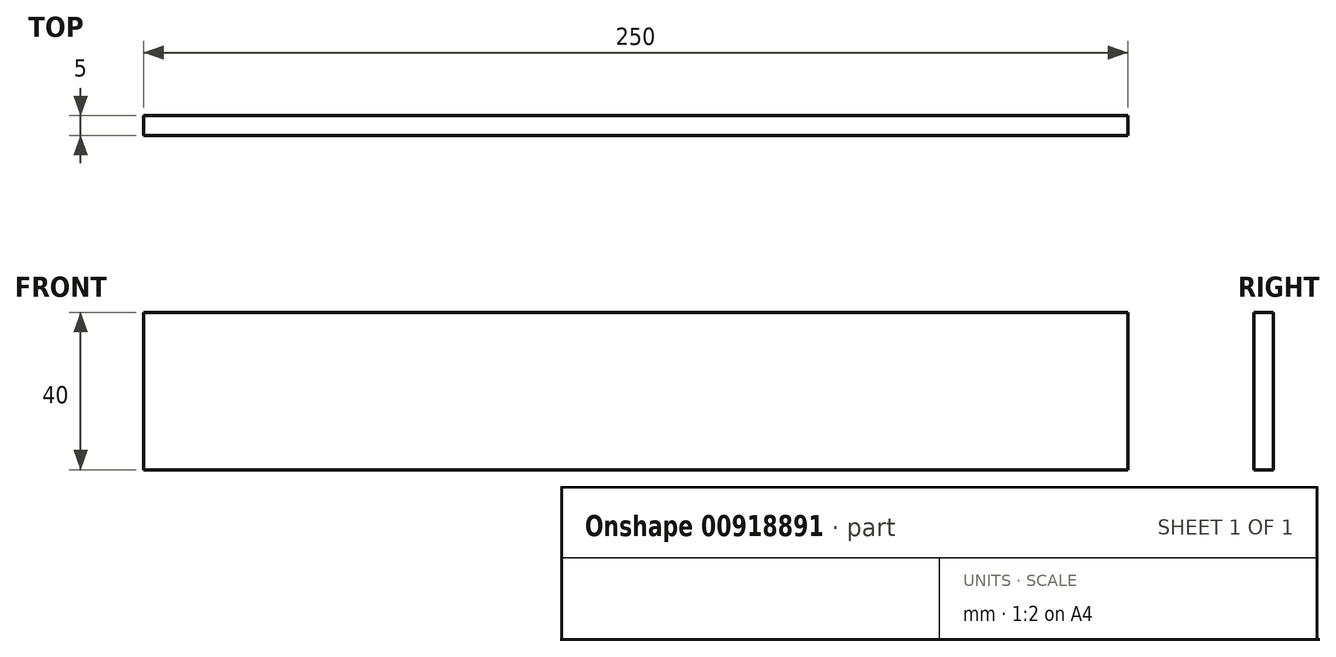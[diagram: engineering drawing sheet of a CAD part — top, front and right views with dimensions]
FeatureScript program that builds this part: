
annotation { "Feature Type Name" : "Feature", "Feature Type Description" : "" }
export const myFeature = defineFeature(function(context is Context, id is Id, definition is map)
    precondition{}
    {
        {
            var Q0;
            Q0=qCreatedBy(makeId("Front.planeOp"),FACE);
            var sketch = newSketch(context, id + "F0", { "sketchPlane" : qUnion([Q0])});
            skLineSegment(sketch, "E0.bottom", {"start": v(-129.94, -72.08) * mm, "end": v(120.06, -72.08) * mm});
            skLineSegment(sketch, "E0.top", {"start": v(-129.94, -112.08) * mm, "end": v(120.06, -112.08) * mm});
            skLineSegment(sketch, "E0.left", {"start": v(-129.94, -72.08) * mm, "end": v(-129.94, -112.08) * mm});
            skLineSegment(sketch, "E0.right", {"start": v(120.06, -72.08) * mm, "end": v(120.06, -112.08) * mm});
            skSolve(sketch);
        }
        {
            var Q0;
            Q0=makeQuery(id+"F0.imprint","IMPRINT",FACE,{"disambiguationData":[TD([[makeQuery(id+"F0.imprint","IMPRINT",EDGE,{"derivedFrom":sQuery(id+"F0.wireOp",EDGE,"E0.bottom")}),-1.0]])]});
            extrude(context, id + "F1", {"entities" : qUnion([Q0]), "depth" : 5 * mm, "offsetDistance" : 25 * mm});
        }
    });
